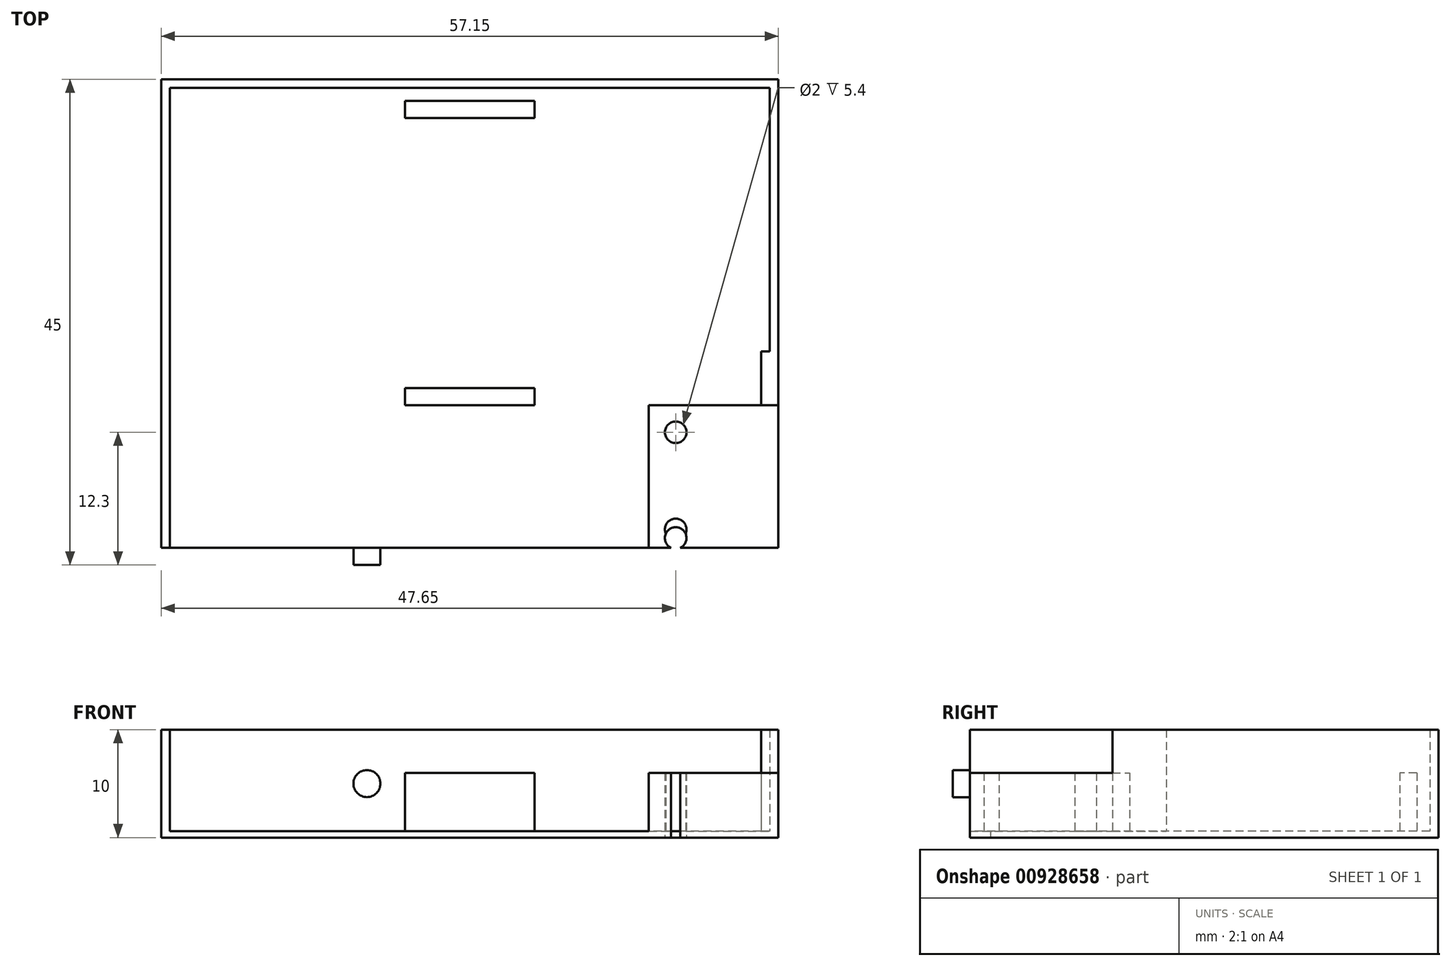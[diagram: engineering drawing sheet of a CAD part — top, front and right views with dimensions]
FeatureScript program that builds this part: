
annotation { "Feature Type Name" : "Feature", "Feature Type Description" : "" }
export const myFeature = defineFeature(function(context is Context, id is Id, definition is map)
    precondition{}
    {
        {
            var Q0;
            Q0=qCreatedBy(makeId("Top.planeOp"),FACE);
            var sketch = newSketch(context, id + "F0", { "sketchPlane" : qUnion([Q0])});
            skLineSegment(sketch, "E0.bottom", {"start": v(0, 0) * mm, "end": v(-57.15, 0) * mm});
            skLineSegment(sketch, "E0.top", {"start": v(0, 45) * mm, "end": v(-57.15, 45) * mm});
            skLineSegment(sketch, "E0.left", {"start": v(0, 0) * mm, "end": v(0, 45) * mm});
            skLineSegment(sketch, "E0.right", {"start": v(-57.15, 0) * mm, "end": v(-57.15, 45) * mm});
            skLineSegment(sketch, "E1.bottom", {"start": v(-34.58, 43) * mm, "end": v(-22.57, 43) * mm});
            skLineSegment(sketch, "E1.top", {"start": v(-34.58, 41.4) * mm, "end": v(-22.57, 41.4) * mm});
            skLineSegment(sketch, "E1.left", {"start": v(-34.58, 43) * mm, "end": v(-34.58, 41.4) * mm});
            skLineSegment(sketch, "E1.right", {"start": v(-22.57, 43) * mm, "end": v(-22.57, 41.4) * mm});
            skLineSegment(sketch, "E2", {"start": v(-34.58, 43) * mm, "end": v(-57.15, 43) * mm});
            skLineSegment(sketch, "E3", {"start": v(-57.15, 43) * mm, "end": v(-22.57, 43) * mm});
            skLineSegment(sketch, "E4", {"start": v(-22.57, 43) * mm, "end": v(0, 43) * mm});
            skLineSegment(sketch, "E5.bottom", {"start": v(-34.58, 14.8) * mm, "end": v(-22.57, 14.8) * mm});
            skLineSegment(sketch, "E5.top", {"start": v(-34.58, 16.4) * mm, "end": v(-22.57, 16.4) * mm});
            skLineSegment(sketch, "E5.left", {"start": v(-34.58, 14.8) * mm, "end": v(-34.58, 16.4) * mm});
            skLineSegment(sketch, "E5.right", {"start": v(-22.57, 14.8) * mm, "end": v(-22.57, 16.4) * mm});
            skLineSegment(sketch, "E6.bottom", {"start": v(0, 0) * mm, "end": v(-12, 0) * mm});
            skLineSegment(sketch, "E6.top", {"start": v(0, 14) * mm, "end": v(-12, 14) * mm});
            skLineSegment(sketch, "E6.left", {"start": v(0, 0) * mm, "end": v(0, 14) * mm});
            skLineSegment(sketch, "E6.right", {"start": v(-12, 0) * mm, "end": v(-12, 14) * mm});
            skLineSegment(sketch, "E7", {"start": v(0, 7) * mm, "end": v(-12, 7) * mm});
            skCircle(sketch, "E8", {"center": v(-9.5, 11.5) * mm, "radius": 1 * mm});
            skCircle(sketch, "E9.MirrorC", {"center": v(-9.5, 2.5) * mm, "radius": 1 * mm});
            skSolve(sketch);
        }
        {
            var Q0;
            {var subQ1=sQuery(id+"F0.wireOp",EDGE,"E0.top");Q0=makeQuery(id+"F0.imprint","IMPRINT",FACE,{"disambiguationData":[TD([[makeQuery(id+"F0.imprint","IMPRINT",EDGE,{"derivedFrom":subQ1}),1.0]])]});}
            var Q1;
            Q1=makeQuery(id+"F0.imprint","IMPRINT",FACE,{"disambiguationData":[TD([[makeQuery(id+"F0.imprint","IMPRINT",EDGE,{"derivedFrom":sQuery(id+"F0.wireOp",EDGE,"E1.top")}),-1.0]])]});
            var Q2;
            Q2=makeQuery(id+"F0.imprint","IMPRINT",FACE,{"disambiguationData":[TD([[makeQuery(id+"F0.imprint","IMPRINT",EDGE,{"derivedFrom":sQuery(id+"F0.wireOp",EDGE,"E1.bottom")}),-1.0]])]});
            var Q3;
            Q3=makeQuery(id+"F0.imprint","IMPRINT",FACE,{"disambiguationData":[TD([[makeQuery(id+"F0.imprint","IMPRINT",EDGE,{"derivedFrom":sQuery(id+"F0.wireOp",EDGE,"E5.bottom")}),1.0]])]});
            var Q4;
            Q4=makeQuery(id+"F0.imprint","IMPRINT",FACE,{"disambiguationData":[TD([[makeQuery(id+"F0.imprint","IMPRINT",EDGE,{"derivedFrom":sQuery(id+"F0.wireOp",EDGE,"E8")}),1.0]])]});
            var Q5;
            {var subQ1=sQuery(id+"F0.wireOp",EDGE,"E6.top");Q5=makeQuery(id+"F0.imprint","IMPRINT",FACE,{"disambiguationData":[TD([[makeQuery(id+"F0.imprint","IMPRINT",EDGE,{"derivedFrom":subQ1}),1.0]])]});}
            var Q6;
            {var subQ0=sQuery(id+"F0.wireOp",EDGE,"E7");Q6=makeQuery(id+"F0.imprint","IMPRINT",FACE,{"disambiguationData":[TD([[makeQuery(id+"F0.imprint","IMPRINT",EDGE,{"derivedFrom":subQ0}),1.0]])]});}
            var Q7;
            Q7=makeQuery(id+"F0.imprint","IMPRINT",FACE,{"disambiguationData":[TD([[makeQuery(id+"F0.imprint","IMPRINT",EDGE,{"derivedFrom":sQuery(id+"F0.wireOp",EDGE,"E9.MirrorC")}),-1.0]])]});
            extrude(context, id + "F1", {"entities" : qUnion([Q0, Q1, Q2, Q3, Q4, Q5, Q6, Q7]), "depth" : 0.6 * mm, "offsetDistance" : 25 * mm});
        }
        {
            var Q0;
            Q0=makeQuery(id+"F1.opExtrude","CAP_FACE",FACE,{"disambiguationData":[OSD([sQuery(id+"F0.wireOp",EDGE,"E0.bottom"),sQuery(id+"F0.wireOp",EDGE,"E0.top"),sQuery(id+"F0.wireOp",EDGE,"E0.left"),sQuery(id+"F0.wireOp",EDGE,"E0.right")])],"isStart":false});
            var sketch = newSketch(context, id + "F2", { "sketchPlane" : qUnion([Q0])});
            skLineSegment(sketch, "E10.bottom", {"start": v(0, 0) * mm, "end": v(-57.15, 0) * mm});
            skLineSegment(sketch, "E10.top", {"start": v(0, 45) * mm, "end": v(-57.15, 45) * mm});
            skLineSegment(sketch, "E10.left", {"start": v(0, 0) * mm, "end": v(0, 45) * mm});
            skLineSegment(sketch, "E10.right", {"start": v(-57.15, 0) * mm, "end": v(-57.15, 45) * mm});
            skLineSegment(sketch, "E11.bottom", {"start": v(-34.57, 43) * mm, "end": v(-22.57, 43) * mm});
            skLineSegment(sketch, "E11.top", {"start": v(-34.58, 41.4) * mm, "end": v(-22.57, 41.4) * mm});
            skLineSegment(sketch, "E11.left", {"start": v(-34.57, 43) * mm, "end": v(-34.57, 41.4) * mm});
            skLineSegment(sketch, "E11.right", {"start": v(-22.57, 43) * mm, "end": v(-22.57, 41.4) * mm});
            skLineSegment(sketch, "E12", {"start": v(-34.57, 43) * mm, "end": v(-57.15, 43) * mm});
            skLineSegment(sketch, "E13", {"start": v(-57.15, 43) * mm, "end": v(-22.57, 43) * mm});
            skLineSegment(sketch, "E14", {"start": v(-22.57, 43) * mm, "end": v(0, 43) * mm});
            skLineSegment(sketch, "E15.bottom", {"start": v(-34.58, 14.8) * mm, "end": v(-22.57, 14.8) * mm});
            skLineSegment(sketch, "E15.top", {"start": v(-34.58, 16.4) * mm, "end": v(-22.57, 16.4) * mm});
            skLineSegment(sketch, "E15.left", {"start": v(-34.58, 14.8) * mm, "end": v(-34.58, 16.4) * mm});
            skLineSegment(sketch, "E15.right", {"start": v(-22.57, 14.8) * mm, "end": v(-22.57, 16.4) * mm});
            skLineSegment(sketch, "E16.bottom", {"start": v(0, 0.8) * mm, "end": v(-12, 0.8) * mm});
            skLineSegment(sketch, "E16.top", {"start": v(0, 14.8) * mm, "end": v(-12, 14.8) * mm});
            skLineSegment(sketch, "E16.left", {"start": v(0, 0.8) * mm, "end": v(0, 14.8) * mm});
            skLineSegment(sketch, "E16.right", {"start": v(-12, 0.8) * mm, "end": v(-12, 14.8) * mm});
            skLineSegment(sketch, "E17", {"start": v(0, 7.8) * mm, "end": v(-12, 7.8) * mm});
            skCircle(sketch, "E18", {"center": v(-9.5, 12.3) * mm, "radius": 1 * mm});
            skCircle(sketch, "E19.MirrorC", {"center": v(-9.5, 3.3) * mm, "radius": 1 * mm});
            skSolve(sketch);
        }
        {
            var Q0;
            Q0=makeQuery(id+"F2.imprint","IMPRINT",FACE,{"disambiguationData":[TD([[makeQuery(id+"F2.imprint","IMPRINT",EDGE,{"derivedFrom":sQuery(id+"F2.wireOp",EDGE,"E11.bottom")}),-1.0]])]});
            var Q1;
            Q1=makeQuery(id+"F2.imprint","IMPRINT",FACE,{"disambiguationData":[TD([[makeQuery(id+"F2.imprint","IMPRINT",EDGE,{"derivedFrom":sQuery(id+"F2.wireOp",EDGE,"E15.bottom")}),1.0]])]});
            var Q2;
            {var subQ1=sQuery(id+"F2.wireOp",EDGE,"3917674d-35bd-4057-851f-c423dae2453d.top");Q2=makeQuery(id+"F2.imprint","IMPRINT",FACE,{"disambiguationData":[TD([[makeQuery(id+"F2.imprint","IMPRINT",EDGE,{"derivedFrom":subQ1}),1.0]])]});}
            var Q3;
            {var subQ2=sQuery(id+"F2.wireOp",EDGE,"3917674d-35bd-4057-851f-c423dae2453d.bottom");Q3=makeQuery(id+"F2.imprint","IMPRINT",FACE,{"disambiguationData":[TD([[makeQuery(id+"F2.imprint","IMPRINT",EDGE,{"derivedFrom":subQ2}),-1.0]])]});}
            var Q4;
            {var subQ2=sQuery(id+"F2.wireOp",EDGE,"E16.top");Q4=makeQuery(id+"F2.imprint","IMPRINT",FACE,{"disambiguationData":[TD([[makeQuery(id+"F2.imprint","IMPRINT",EDGE,{"derivedFrom":subQ2}),1.0]])]});}
            var Q5;
            {var subQ1=sQuery(id+"F2.wireOp",EDGE,"E16.bottom");Q5=makeQuery(id+"F2.imprint","IMPRINT",FACE,{"disambiguationData":[TD([[makeQuery(id+"F2.imprint","IMPRINT",EDGE,{"derivedFrom":subQ1}),-1.0]])]});}
            extrude(context, id + "F3", {"entities" : qUnion([Q0, Q1, Q2, Q3, Q4, Q5]), "operationType" : NewBodyOperationType.ADD, "depth" : 5.4 * mm, "offsetDistance" : 25 * mm});
        }
        {
            var Q0;
            {var subQ0=sQuery(id+"F0.wireOp",EDGE,"E0.left");var subQ1=sQuery(id+"F0.wireOp",EDGE,"E0.bottom");var subQ2=sQuery(id+"F0.wireOp",EDGE,"E0.right");var subQ3=sQuery(id+"F0.wireOp",EDGE,"E0.top");Q0=makeQuery(id+"F3.boolean.opBoolean","SPLIT",FACE,{"disambiguationData":[TD([makeQuery(id+"F1.opExtrude","SWEPT_FACE",FACE,{"disambiguationData":[OSD([subQ1])]})])],"derivedFrom":makeQuery(id+"F1.opExtrude","CAP_FACE",FACE,{"disambiguationData":[OSD([subQ1,subQ3,subQ0,subQ2])],"isStart":false})});}
            var sketch = newSketch(context, id + "F4", { "sketchPlane" : qUnion([Q0])});
            skLineSegment(sketch, "E20.bottom", {"start": v(-57.15, 45) * mm, "end": v(0, 45) * mm});
            skLineSegment(sketch, "E20.top", {"start": v(-57.15, 0) * mm, "end": v(0, 0) * mm});
            skLineSegment(sketch, "E20.left", {"start": v(-57.15, 45) * mm, "end": v(-57.15, 0) * mm});
            skLineSegment(sketch, "E20.right", {"start": v(0, 45) * mm, "end": v(0, 0) * mm});
            skLineSegment(sketch, "E21.0", {"start": v(-56.35, 44.2) * mm, "end": v(-0.8, 44.2) * mm});
            skLineSegment(sketch, "E21.1", {"start": v(-56.35, 44.2) * mm, "end": v(-56.35, 0.8) * mm});
            skLineSegment(sketch, "E21.3", {"start": v(-0.8, 44.2) * mm, "end": v(-0.8, 0.8) * mm});
            skLineSegment(sketch, "E22", {"start": v(-28.57, 0.8) * mm, "end": v(-28.57, 14.8) * mm});
            skLineSegment(sketch, "E23", {"start": v(-47.62, 0.8) * mm, "end": v(-47.62, 14.8) * mm});
            skLineSegment(sketch, "E24", {"start": v(-28.57, 0.8) * mm, "end": v(-31.07, 0.8) * mm});
            skLineSegment(sketch, "E25", {"start": v(-31.07, 0.8) * mm, "end": v(-31.07, 0) * mm});
            skLineSegment(sketch, "E26", {"start": v(-31.07, 0) * mm, "end": v(-26.07, 0) * mm});
            skLineSegment(sketch, "E27", {"start": v(-26.07, 0) * mm, "end": v(-26.07, 0.8) * mm});
            skLineSegment(sketch, "E28", {"start": v(-26.07, 0.8) * mm, "end": v(-28.57, 0.8) * mm});
            skLineSegment(sketch, "E29", {"start": v(-47.62, 0.8) * mm, "end": v(-45.13, 0.8) * mm});
            skLineSegment(sketch, "E30", {"start": v(-45.13, 0.8) * mm, "end": v(-45.13, 0) * mm});
            skLineSegment(sketch, "E31", {"start": v(-45.13, 0) * mm, "end": v(-50.12, 0) * mm});
            skLineSegment(sketch, "E32", {"start": v(-50.12, 0) * mm, "end": v(-50.12, 0.8) * mm});
            skLineSegment(sketch, "E33", {"start": v(-50.12, 0.8) * mm, "end": v(-47.62, 0.8) * mm});
            skLineSegment(sketch, "E34", {"start": v(-56.35, 0.8) * mm, "end": v(-50.12, 0.8) * mm});
            skLineSegment(sketch, "E35", {"start": v(-45.13, 0.8) * mm, "end": v(-31.07, 0.8) * mm});
            skLineSegment(sketch, "E36", {"start": v(-26.07, 0.8) * mm, "end": v(-12, 0.8) * mm});
            skLineSegment(sketch, "E37", {"start": v(-12, 0.8) * mm, "end": v(-0.8, 0.8) * mm});
            skLineSegment(sketch, "E38.MirrorCS", {"start": v(-12.02, 0.8) * mm, "end": v(-12.02, 0) * mm});
            skLineSegment(sketch, "E39.MirrorCS", {"start": v(-9.52, 0.8) * mm, "end": v(-12.02, 0.8) * mm});
            skLineSegment(sketch, "E40.MirrorCS", {"start": v(-7.02, 0.8) * mm, "end": v(-9.52, 0.8) * mm});
            skLineSegment(sketch, "E41.MirrorCS", {"start": v(-7.02, 0) * mm, "end": v(-7.02, 0.8) * mm});
            skLineSegment(sketch, "E42", {"start": v(-38.1, 0.8) * mm, "end": v(-38.1, 1.6) * mm});
            skLineSegment(sketch, "E43", {"start": v(-38.1, 1.6) * mm, "end": v(-40.6, 1.6) * mm});
            skLineSegment(sketch, "E44", {"start": v(-40.6, 1.6) * mm, "end": v(-40.6, 0.8) * mm});
            skLineSegment(sketch, "E45", {"start": v(-40.6, 0.8) * mm, "end": v(-38.1, 0.8) * mm});
            skLineSegment(sketch, "E46", {"start": v(-38.1, 0.8) * mm, "end": v(-35.6, 0.8) * mm});
            skLineSegment(sketch, "E47", {"start": v(-35.6, 0.8) * mm, "end": v(-35.6, 1.6) * mm});
            skLineSegment(sketch, "E48", {"start": v(-35.6, 1.6) * mm, "end": v(-38.1, 1.6) * mm});
            skLineSegment(sketch, "E49.MirrorCS", {"start": v(-21.55, 0.8) * mm, "end": v(-21.55, 1.6) * mm});
            skLineSegment(sketch, "E50.MirrorCS", {"start": v(-21.55, 1.6) * mm, "end": v(-19.05, 1.6) * mm});
            skLineSegment(sketch, "E51.MirrorCS", {"start": v(-19.05, 1.6) * mm, "end": v(-16.55, 1.6) * mm});
            skLineSegment(sketch, "E52.MirrorCS", {"start": v(-16.55, 1.6) * mm, "end": v(-16.55, 0.8) * mm});
            skLineSegment(sketch, "E53.bottom", {"start": v(-0.8, 0.8) * mm, "end": v(0, 0.8) * mm});
            skLineSegment(sketch, "E53.top", {"start": v(-0.8, 14.8) * mm, "end": v(0, 14.8) * mm});
            skLineSegment(sketch, "E53.left", {"start": v(-0.8, 0.8) * mm, "end": v(-0.8, 14.8) * mm});
            skLineSegment(sketch, "E53.right", {"start": v(0, 0.8) * mm, "end": v(0, 14.8) * mm});
            skLineSegment(sketch, "E54.bottom", {"start": v(-0.8, 14.8) * mm, "end": v(-1.6, 14.8) * mm});
            skLineSegment(sketch, "E54.top", {"start": v(-0.8, 19.8) * mm, "end": v(-1.6, 19.8) * mm});
            skLineSegment(sketch, "E54.left", {"start": v(-0.8, 14.8) * mm, "end": v(-0.8, 19.8) * mm});
            skLineSegment(sketch, "E54.right", {"start": v(-1.6, 14.8) * mm, "end": v(-1.6, 19.8) * mm});
            skSolve(sketch);
        }
        {
            var Q0;
            {var subQ1=sQuery(id+"F4.wireOp",EDGE,"E25");Q0=makeQuery(id+"F4.imprint","IMPRINT",FACE,{"disambiguationData":[TD([[makeQuery(id+"F4.imprint","IMPRINT",EDGE,{"derivedFrom":subQ1}),-1.0]])]});}
            var Q1;
            {var subQ2=sQuery(id+"F4.wireOp",EDGE,"E42");Q1=makeQuery(id+"F4.imprint","IMPRINT",FACE,{"disambiguationData":[TD([[makeQuery(id+"F4.imprint","IMPRINT",EDGE,{"derivedFrom":subQ2}),-1.0]])]});}
            var Q2;
            {var subQ0=sQuery(id+"F4.wireOp",EDGE,"E42");Q2=makeQuery(id+"F4.imprint","IMPRINT",FACE,{"disambiguationData":[TD([[makeQuery(id+"F4.imprint","IMPRINT",EDGE,{"derivedFrom":subQ0}),1.0]])]});}
            var Q3;
            {var subQ0=sQuery(id+"F4.wireOp",EDGE,"E49.MirrorCS");Q3=makeQuery(id+"F4.imprint","IMPRINT",FACE,{"disambiguationData":[TD([[makeQuery(id+"F4.imprint","IMPRINT",EDGE,{"derivedFrom":subQ0}),-1.0]])]});}
            var Q4;
            {var subQ1=sQuery(id+"F4.wireOp",EDGE,"E27");Q4=makeQuery(id+"F4.imprint","IMPRINT",FACE,{"disambiguationData":[TD([[makeQuery(id+"F4.imprint","IMPRINT",EDGE,{"derivedFrom":subQ1}),-1.0]])]});}
            var Q5;
            {var subQ0=sQuery(id+"F4.wireOp",EDGE,"E41.MirrorCS");Q5=makeQuery(id+"F4.imprint","IMPRINT",FACE,{"disambiguationData":[TD([[makeQuery(id+"F4.imprint","IMPRINT",EDGE,{"derivedFrom":subQ0}),-1.0]])]});}
            var Q6;
            {var subQ5=sQuery(id+"F4.wireOp",EDGE,"E20.bottom");Q6=makeQuery(id+"F4.imprint","IMPRINT",FACE,{"disambiguationData":[TD([[makeQuery(id+"F4.imprint","IMPRINT",EDGE,{"derivedFrom":subQ5}),1.0]])]});}
            var Q7;
            {var subQ0=sQuery(id+"F4.wireOp",EDGE,"E54.bottom");Q7=makeQuery(id+"F4.imprint","IMPRINT",FACE,{"disambiguationData":[TD([[makeQuery(id+"F4.imprint","IMPRINT",EDGE,{"derivedFrom":subQ0}),-1.0]])]});}
            extrude(context, id + "F5", {"entities" : qUnion([Q0, Q1, Q2, Q3, Q4, Q5, Q6, Q7]), "operationType" : NewBodyOperationType.ADD, "depth" : 9.4 * mm, "offsetDistance" : 25 * mm});
        }
        {
            var Q0;
            Q0=makeQuery(id+"F4.imprint","IMPRINT",FACE,{"disambiguationData":[TD([[makeQuery(id+"F4.imprint","IMPRINT",EDGE,{"derivedFrom":sQuery(id+"F4.wireOp",EDGE,"E24")}),1.0]])]});
            var Q1;
            Q1=makeQuery(id+"F4.imprint","IMPRINT",FACE,{"disambiguationData":[TD([[makeQuery(id+"F4.imprint","IMPRINT",EDGE,{"derivedFrom":sQuery(id+"F4.wireOp",EDGE,"E29")}),-1.0]])]});
            var Q2;
            {var subQ5=sQuery(id+"F4.wireOp",EDGE,"E38.MirrorCS");Q2=makeQuery(id+"F4.imprint","IMPRINT",FACE,{"disambiguationData":[TD([[makeQuery(id+"F4.imprint","IMPRINT",EDGE,{"derivedFrom":subQ5}),1.0]])]});}
            extrude(context, id + "F6", {"entities" : qUnion([Q0, Q1, Q2]), "operationType" : NewBodyOperationType.ADD, "depth" : 4.4 * mm, "offsetDistance" : 25 * mm});
        }
        {
            var Q0;
            Q0=makeQuery(id+"F6.opExtrude","CAP_FACE",FACE,{"disambiguationData":[OSD([sQuery(id+"F4.wireOp",EDGE,"E20.top"),sQuery(id+"F4.wireOp",EDGE,"E36"),sQuery(id+"F4.wireOp",EDGE,"E37"),sQuery(id+"F4.wireOp",EDGE,"E38.MirrorCS"),sQuery(id+"F4.wireOp",EDGE,"E41.MirrorCS")])],"isStart":false});
            extrude(context, id + "F7", {"entities" : qUnion([Q0]), "operationType" : NewBodyOperationType.ADD, "depth" : 1 * mm, "offsetDistance" : 25 * mm});
        }
        {
            var Q0;
            {var subQ0=sQuery(id+"F4.wireOp",EDGE,"E20.top");var subQ1=makeQuery(id+"F4.imprint","INTERSECT",VERTEX,{"derivedFrom":[subQ0,sQuery(id+"F4.wireOp",EDGE,"E30")]});var subQ3=makeQuery(id+"F4.imprint","INTERSECT",VERTEX,{"derivedFrom":[subQ0,sQuery(id+"F4.wireOp",EDGE,"E25")]});var subQ4=makeQuery(id+"F4.imprint","INTERSECT",VERTEX,{"derivedFrom":[subQ0,sQuery(id+"F4.wireOp",EDGE,"E27")]});var subQ5=makeQuery(id+"F4.imprint","INTERSECT",VERTEX,{"derivedFrom":[subQ0,sQuery(id+"F4.wireOp",EDGE,"E38.MirrorCS")]});Q0=makeQuery(id+"F7.boolean.opBoolean","MERGE",FACE,{"derivedFrom":[makeQuery(id+"F6.boolean.opBoolean","MERGE",FACE,{"derivedFrom":[makeQuery(id+"F5.boolean.opBoolean","MERGE",FACE,{"derivedFrom":[makeQuery(id+"F1.opExtrude","SWEPT_FACE",FACE,{"disambiguationData":[OSD([sQuery(id+"F0.wireOp",EDGE,"E0.bottom")])]}),makeQuery(id+"F5.opExtrude","SWEPT_FACE",FACE,{"disambiguationData":[OSD([subQ0]),TDD([makeQuery(id+"F4.imprint","IMPRINT",EDGE,{"disambiguationData":[TD([[makeQuery(id+"F4.imprint","INTERSECT",VERTEX,{"derivedFrom":[subQ0,sQuery(id+"F4.wireOp",EDGE,"E20.right")]}),-1.0]])],"derivedFrom":subQ0})])]}),makeQuery(id+"F5.opExtrude","SWEPT_FACE",FACE,{"disambiguationData":[OSD([subQ0]),TDD([makeQuery(id+"F4.imprint","IMPRINT",EDGE,{"disambiguationData":[TD([[subQ4,1.0]])],"derivedFrom":subQ0})])]}),makeQuery(id+"F5.opExtrude","SWEPT_FACE",FACE,{"disambiguationData":[OSD([subQ0]),TDD([makeQuery(id+"F4.imprint","IMPRINT",EDGE,{"disambiguationData":[TD([[subQ3,-1.0]])],"derivedFrom":subQ0})])]}),makeQuery(id+"F5.opExtrude","SWEPT_FACE",FACE,{"disambiguationData":[OSD([subQ0]),TDD([makeQuery(id+"F4.imprint","IMPRINT",EDGE,{"disambiguationData":[TD([[makeQuery(id+"F4.imprint","INTERSECT",VERTEX,{"derivedFrom":[subQ0,sQuery(id+"F4.wireOp",EDGE,"E20.left")]}),1.0]])],"derivedFrom":subQ0})])]})]}),makeQuery(id+"F6.opExtrude","SWEPT_FACE",FACE,{"disambiguationData":[OSD([subQ0]),TDD([makeQuery(id+"F4.imprint","IMPRINT",EDGE,{"disambiguationData":[TD([[subQ5,1.0]])],"derivedFrom":subQ0})])]}),makeQuery(id+"F6.opExtrude","SWEPT_FACE",FACE,{"disambiguationData":[OSD([subQ0]),TDD([makeQuery(id+"F4.imprint","IMPRINT",EDGE,{"disambiguationData":[TD([[subQ3,1.0]])],"derivedFrom":subQ0})])]}),makeQuery(id+"F6.opExtrude","SWEPT_FACE",FACE,{"disambiguationData":[OSD([subQ0]),TDD([makeQuery(id+"F4.imprint","IMPRINT",EDGE,{"disambiguationData":[TD([[subQ1,-1.0]])],"derivedFrom":subQ0})])]})]}),makeQuery(id+"F7.opExtrude","SWEPT_FACE",FACE,{"disambiguationData":[OSD([subQ0])]})]});}
            var sketch = newSketch(context, id + "F8", { "sketchPlane" : qUnion([Q0])});
            skLineSegment(sketch, "E55", {"start": v(-19.05, 10) * mm, "end": v(-19.05, 5) * mm});
            skCircle(sketch, "E56", {"center": v(-19.05, 5) * mm, "radius": 1.25 * mm});
            skLineSegment(sketch, "E57", {"start": v(-28.57, 5) * mm, "end": v(-28.57, 10) * mm});
            skCircle(sketch, "E58.MirrorC", {"center": v(-38.1, 5) * mm, "radius": 1.25 * mm});
            skSolve(sketch);
        }
        {
            var Q0;
            Q0=makeQuery(id+"F8.imprint","IMPRINT",FACE,{"disambiguationData":[TD([[makeQuery(id+"F8.imprint","IMPRINT",EDGE,{"derivedFrom":sQuery(id+"F8.wireOp",EDGE,"E58.MirrorC")}),-1.0]])]});
            var Q1;
            Q1=makeQuery(id+"F8.imprint","IMPRINT",FACE,{"disambiguationData":[TD([[makeQuery(id+"F8.imprint","IMPRINT",EDGE,{"derivedFrom":sQuery(id+"F8.wireOp",EDGE,"E56")}),1.0]])]});
            extrude(context, id + "F9", {"entities" : qUnion([Q0, Q1]), "operationType" : NewBodyOperationType.REMOVE, "oppositeDirection" : true, "depth" : 1.6 * mm, "offsetDistance" : 25 * mm});
        }
    });
